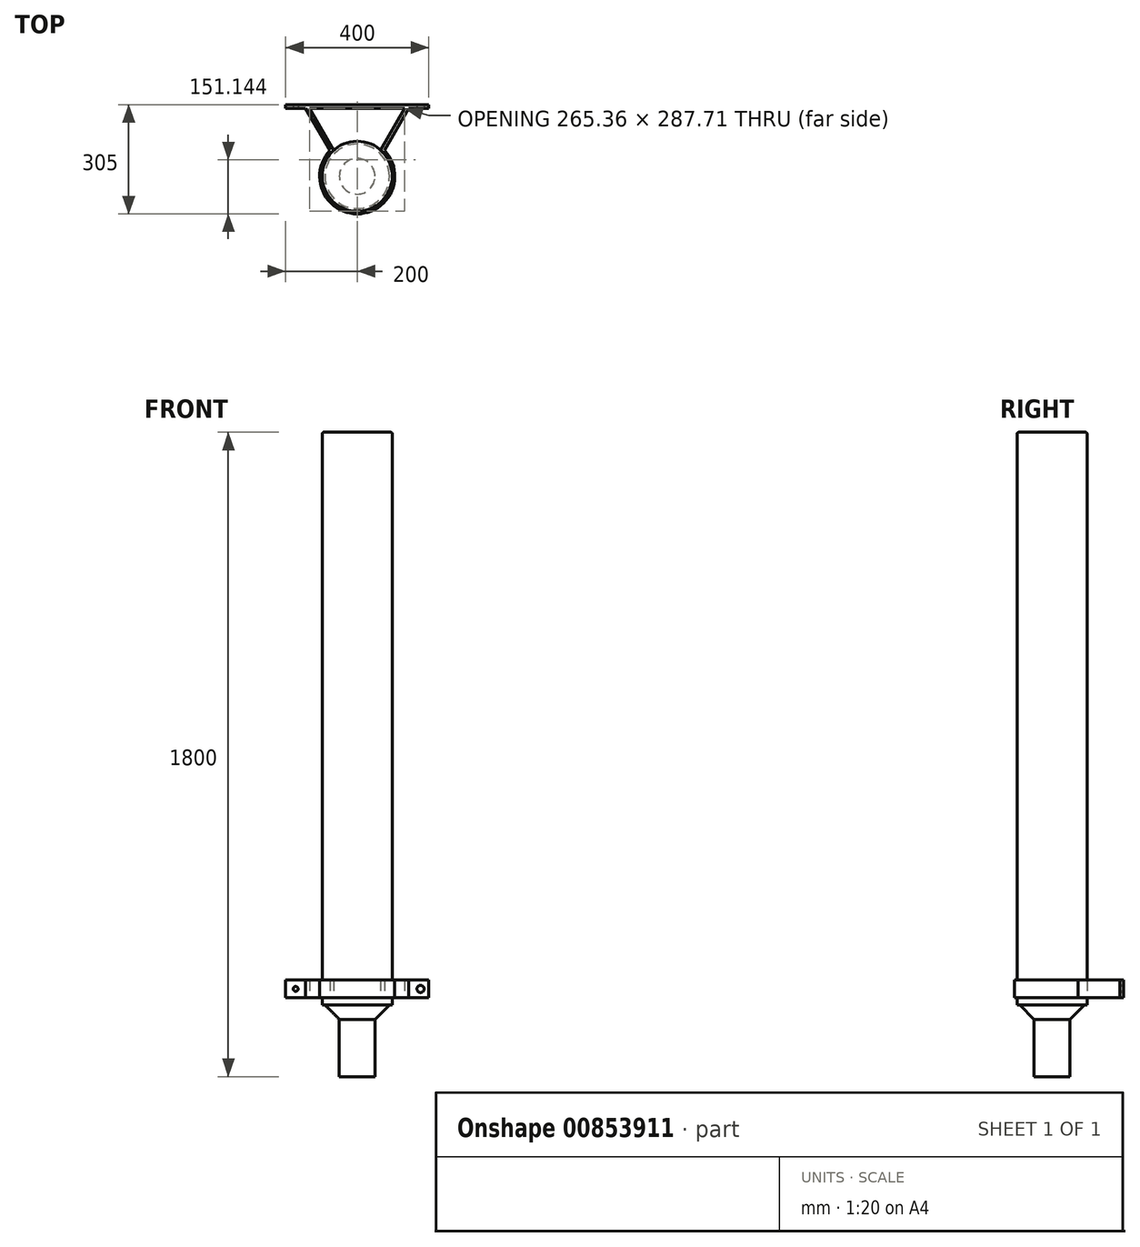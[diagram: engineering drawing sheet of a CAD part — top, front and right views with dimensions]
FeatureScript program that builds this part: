
annotation { "Feature Type Name" : "Feature", "Feature Type Description" : "" }
export const myFeature = defineFeature(function(context is Context, id is Id, definition is map)
    precondition{}
    {
        {
            var Q0;
            Q0=qCreatedBy(makeId("Top.planeOp"),FACE);
            var sketch = newSketch(context, id + "F0", { "sketchPlane" : qUnion([Q0])});
            skCircle(sketch, "E0", {"center": v(0, 0) * mm, "radius": 98 * mm});
            skSolve(sketch);
        }
        {
            var Q0;
            Q0=makeQuery(id+"F0.imprint","IMPRINT",FACE,{"disambiguationData":[TD([[makeQuery(id+"F0.imprint","IMPRINT",EDGE,{"derivedFrom":sQuery(id+"F0.wireOp",EDGE,"E0")}),1.0]])]});
            extrude(context, id + "F1", {"entities" : qUnion([Q0]), "endBound" : BoundingType.SYMMETRIC, "offsetDistance" : 25 * mm, "depth" : 1800 * mm});
        }
        {
            var Q0;
            Q0=makeQuery(id+"F1.opExtrude","CAP_FACE",FACE,{"disambiguationData":[OSD([sQuery(id+"F0.wireOp",EDGE,"E0")])],"isStart":true});
            var sketch = newSketch(context, id + "F2", { "sketchPlane" : qUnion([Q0])});
            skCircle(sketch, "E1", {"center": v(0, 0) * mm, "radius": 50 * mm});
            skCircle(sketch, "E2.0", {"center": v(0, 0) * mm, "radius": 98 * mm});
            skSolve(sketch);
        }
        {
            var Q0;
            Q0=makeQuery(id+"F2.imprint","IMPRINT",FACE,{"disambiguationData":[TD([[makeQuery(id+"F2.imprint","IMPRINT",EDGE,{"derivedFrom":sQuery(id+"F2.wireOp",EDGE,"E1")}),-1.0]])]});
            extrude(context, id + "F3", {"entities" : qUnion([Q0]), "operationType" : NewBodyOperationType.REMOVE, "oppositeDirection" : true, "depth" : 200 * mm});
        }
        {
            var Q0;
            Q0=makeQuery(id+"F3.boolean.opBoolean","COPY",EDGE,{"derivedFrom":makeQuery(id+"F3.opExtrude","CAP_EDGE",EDGE,{"disambiguationData":[OSD([sQuery(id+"F2.wireOp",EDGE,"E1")])],"isStart":false})});
            chamfer(context, id + "F4", {"entities" : qUnion([Q0]), "width" : 40 * mm, "tangentPropagation" : true});
        }
        {
            var Q0;
            Q0=makeQuery(id+"F3.boolean.opBoolean","COPY",EDGE,{"derivedFrom":makeQuery(id+"F3.opExtrude","CAP_EDGE",EDGE,{"disambiguationData":[OSD([sQuery(id+"F2.wireOp",EDGE,"E1")])],"isStart":true})});
            var Q1;
            Q1=makeQuery(id+"F1.opExtrude","CAP_EDGE",EDGE,{"disambiguationData":[OSD([sQuery(id+"F0.wireOp",EDGE,"E0")])],"isStart":false});
            fillet(context, id + "F5", {"entities" : qUnion([Q0, Q1]), "radius" : 5 * mm, "tangentPropagation" : true, "allowEdgeOverflow" : false});
        }
        {
            var Q0;
            Q0=makeQuery(id+"F1.opExtrude","CAP_FACE",FACE,{"disambiguationData":[OSD([sQuery(id+"F0.wireOp",EDGE,"E0")])],"isStart":true});
            cPlane(context, id + "F6", {"entities" : qUnion([Q0]), "cplaneType" : CPlaneType.OFFSET, "offset" : 220 * mm, "oppositeDirection" : true, "width" : 150 * mm, "height" : 150 * mm});
        }
        {
            var Q0;
            Q0=qCreatedBy(id+"F6.planeOp",FACE);
            var sketch = newSketch(context, id + "F7", { "sketchPlane" : qUnion([Q0])});
            skArc(sketch, "E3.0", {"start": v(65.22, -73.15) * mm, "mid": v(0, 98) * mm, "end": v(-65.22, -73.15) * mm});
            skLineSegment(sketch, "E4", {"start": v(-65.22, -73.15) * mm, "end": v(-132.68, -190) * mm});
            skLineSegment(sketch, "E5", {"start": v(-132.68, -190) * mm, "end": v(132.68, -190) * mm});
            skLineSegment(sketch, "E6", {"start": v(132.68, -190) * mm, "end": v(65.22, -73.15) * mm});
            skArc(sketch, "E7", {"start": v(76.22, -72.22) * mm, "mid": v(0, 105) * mm, "end": v(-76.22, -72.22) * mm});
            skLineSegment(sketch, "E8", {"start": v(144.23, -190) * mm, "end": v(76.22, -72.22) * mm});
            skLineSegment(sketch, "E9", {"start": v(-76.22, -72.22) * mm, "end": v(-144.23, -190) * mm});
            skLineSegment(sketch, "E10", {"start": v(-150, -200) * mm, "end": v(150, -200) * mm});
            skLineSegment(sketch, "E11", {"start": v(-76.22, -72.22) * mm, "end": v(-65.22, -73.15) * mm});
            skLineSegment(sketch, "E12", {"start": v(76.22, -72.22) * mm, "end": v(65.22, -73.15) * mm});
            skLineSegment(sketch, "E13", {"start": v(-150, -200) * mm, "end": v(-200, -200) * mm});
            skLineSegment(sketch, "E14", {"start": v(-200, -200) * mm, "end": v(-200, -190) * mm});
            skLineSegment(sketch, "E15", {"start": v(-200, -190) * mm, "end": v(-144.23, -190) * mm});
            skLineSegment(sketch, "E16", {"start": v(150, -200) * mm, "end": v(200, -200) * mm});
            skLineSegment(sketch, "E17", {"start": v(200, -200) * mm, "end": v(200, -190) * mm});
            skLineSegment(sketch, "E18", {"start": v(200, -190) * mm, "end": v(144.23, -190) * mm});
            skSolve(sketch);
        }
        {
            var Q0;
            Q0=makeQuery(id+"F7.imprint","IMPRINT",FACE,{"disambiguationData":[TD([[makeQuery(id+"F7.imprint","IMPRINT",EDGE,{"derivedFrom":sQuery(id+"F7.wireOp",EDGE,"E4")}),-1.0]])]});
            var Q1;
            Q1=makeQuery(id+"F7.imprint","IMPRINT",FACE,{"disambiguationData":[TD([[makeQuery(id+"F7.imprint","IMPRINT",EDGE,{"derivedFrom":sQuery(id+"F7.wireOp",EDGE,"E3.0")}),-1.0]])]});
            extrude(context, id + "F8", {"entities" : qUnion([Q0, Q1]), "operationType" : NewBodyOperationType.ADD, "oppositeDirection" : true, "offsetDistance" : 25 * mm, "depth" : 50 * mm});
        }
        {
            var Q0;
            Q0=makeQuery(id+"F8.opExtrude","SWEPT_FACE",FACE,{"disambiguationData":[OSD([sQuery(id+"F7.wireOp",EDGE,"E15")])]});
            var sketch = newSketch(context, id + "F9", { "sketchPlane" : qUnion([Q0])});
            skCircle(sketch, "E19", {"center": v(-172.11, -655) * mm, "radius": 6.75 * mm});
            skPoint(sketch, "E19.centerSnap0", {"position": v(-172.11, -630) * mm});
            skPoint(sketch, "E19.centerSnap1", {"position": v(-200, -655) * mm});
            skCircle(sketch, "E20", {"center": v(176.86, -655) * mm, "radius": 10 * mm});
            skSolve(sketch);
        }
        {
            var Q0;
            Q0=makeQuery(id+"F9.imprint","IMPRINT",FACE,{"disambiguationData":[TD([[makeQuery(id+"F9.imprint","IMPRINT",EDGE,{"derivedFrom":sQuery(id+"F9.wireOp",EDGE,"E19")}),1.0]])]});
            var Q1;
            Q1=makeQuery(id+"F9.imprint","IMPRINT",FACE,{"disambiguationData":[TD([[makeQuery(id+"F9.imprint","IMPRINT",EDGE,{"derivedFrom":sQuery(id+"F9.wireOp",EDGE,"E20")}),1.0]])]});
            extrude(context, id + "F10", {"entities" : qUnion([Q0, Q1]), "operationType" : NewBodyOperationType.REMOVE, "endBound" : BoundingType.THROUGH_ALL, "oppositeDirection" : true, "depth" : 25 * mm});
        }
        {
            var Q0;
            Q0=qCreatedBy(id+"F6.planeOp",FACE);
            cPlane(context, id + "F11", {"entities" : qUnion([Q0]), "cplaneType" : CPlaneType.OFFSET, "offset" : 750 * mm, "oppositeDirection" : true, "width" : 150 * mm, "height" : 150 * mm});
        }
    });
